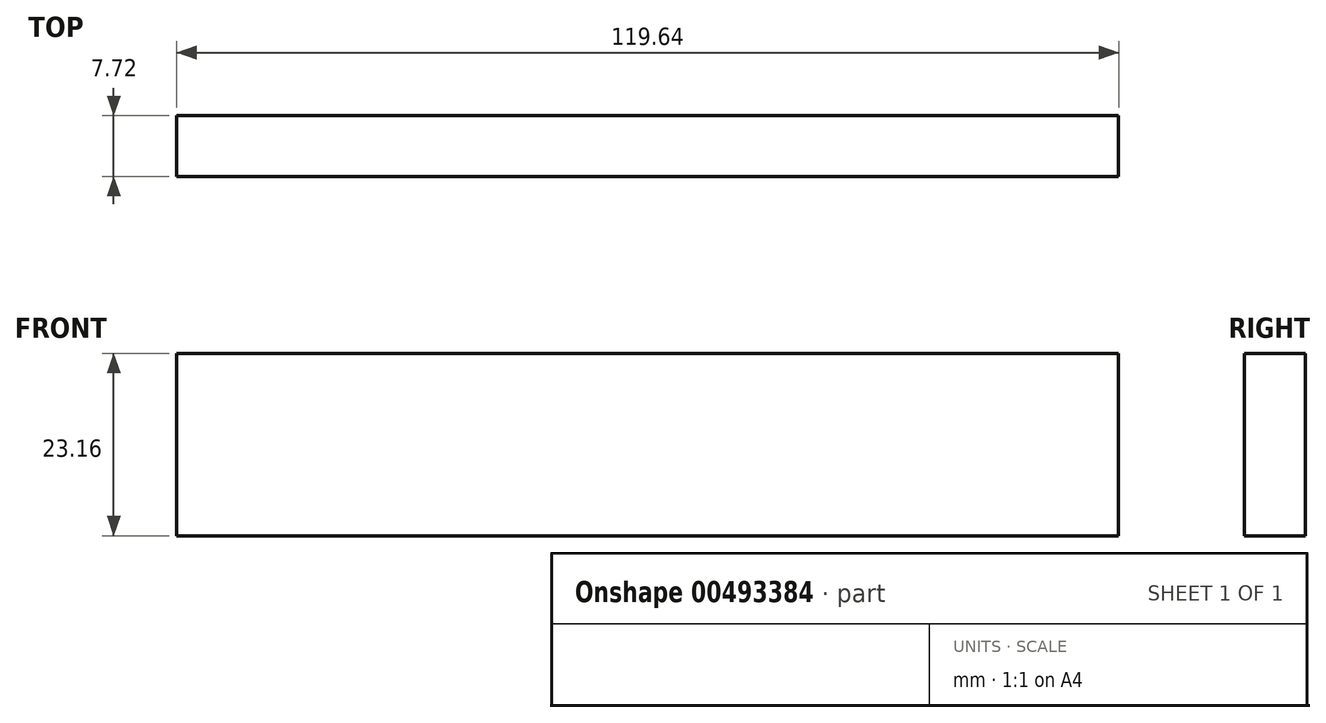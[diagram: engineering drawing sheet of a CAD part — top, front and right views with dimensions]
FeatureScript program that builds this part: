
annotation { "Feature Type Name" : "Feature", "Feature Type Description" : "" }
export const myFeature = defineFeature(function(context is Context, id is Id, definition is map)
    precondition{}
    {
        {
            var Q0;
            Q0=qCreatedBy(makeId("Front.planeOp"),FACE);
            var sketch = newSketch(context, id + "F0", { "sketchPlane" : qUnion([Q0])});
            skLineSegment(sketch, "E0.bottom", {"start": v(-59.82, 11.58) * mm, "end": v(59.82, 11.58) * mm});
            skLineSegment(sketch, "E0.top", {"start": v(-59.82, -11.58) * mm, "end": v(59.82, -11.58) * mm});
            skLineSegment(sketch, "E0.left", {"start": v(-59.82, 11.58) * mm, "end": v(-59.82, -11.58) * mm});
            skLineSegment(sketch, "E0.right", {"start": v(59.82, 11.58) * mm, "end": v(59.82, -11.58) * mm});
            skPoint(sketch, "E0.middle", {"position": v(0, 0) * mm});
            skSolve(sketch);
        }
        {
            var Q0;
            Q0 = qSketchRegion(id + "F0", true);
            extrude(context, id + "F1", {"entities" : qUnion([Q0]), "depth" : 7.72 * mm});
        }
    });
